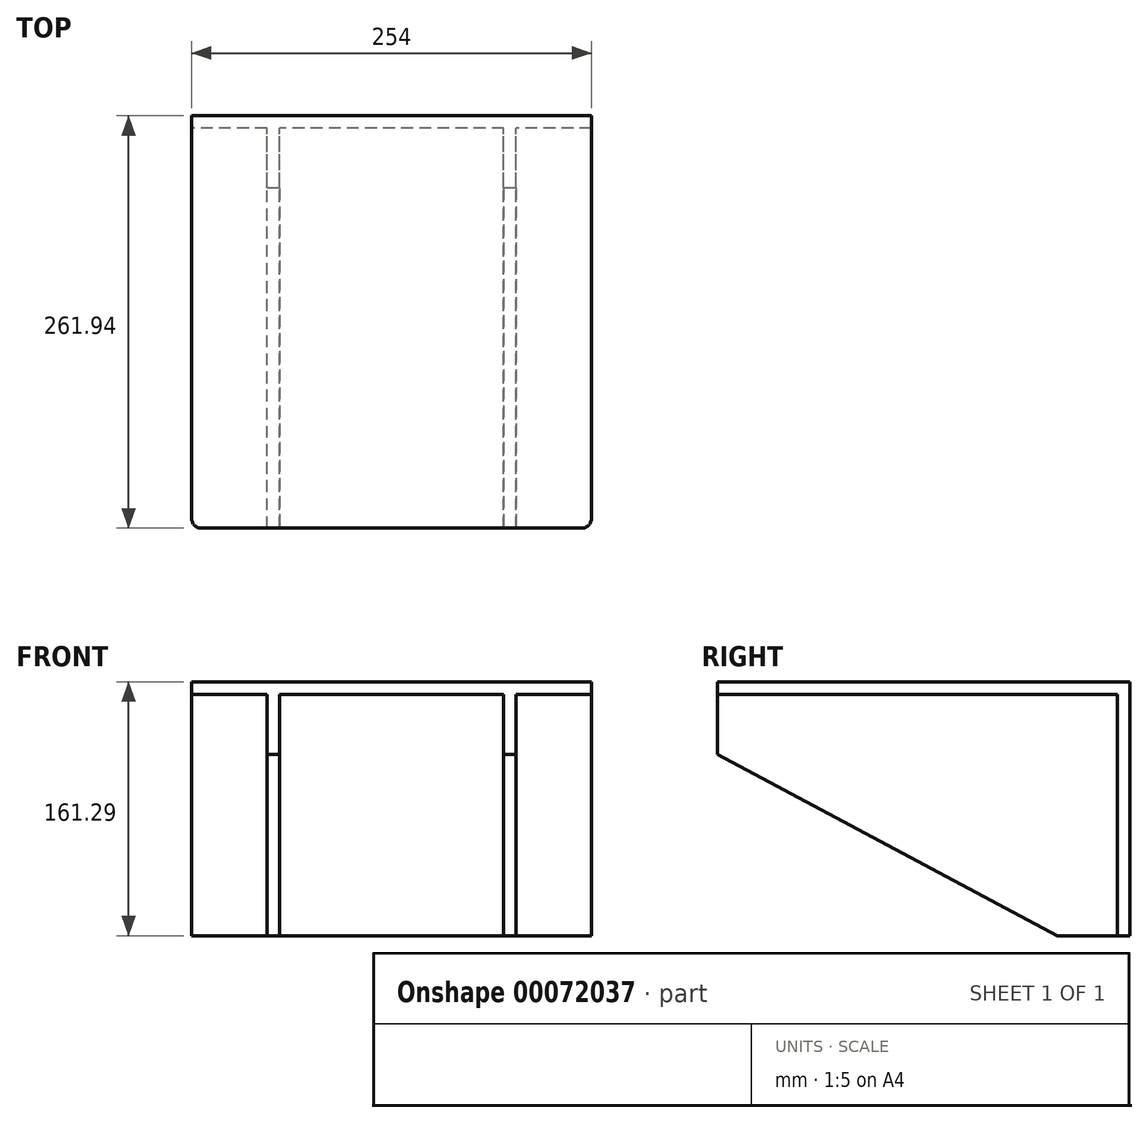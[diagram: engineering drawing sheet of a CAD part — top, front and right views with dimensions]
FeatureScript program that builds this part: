
annotation { "Feature Type Name" : "Feature", "Feature Type Description" : "" }
export const myFeature = defineFeature(function(context is Context, id is Id, definition is map)
    precondition{}
    {
        {
            var Q0;
            Q0=qCreatedBy(makeId("Front.planeOp"),FACE);
            var sketch = newSketch(context, id + "F0", { "sketchPlane" : qUnion([Q0])});
            skLineSegment(sketch, "E0.bottom", {"start": v(127, 80.65) * mm, "end": v(-127, 80.65) * mm});
            skLineSegment(sketch, "E0.top", {"start": v(127, -80.65) * mm, "end": v(-127, -80.65) * mm});
            skLineSegment(sketch, "E0.left", {"start": v(127, 80.65) * mm, "end": v(127, -80.65) * mm});
            skLineSegment(sketch, "E0.right", {"start": v(-127, 80.65) * mm, "end": v(-127, -80.65) * mm});
            skPoint(sketch, "E0.middle", {"position": v(0, 0) * mm});
            skSolve(sketch);
        }
        {
            var Q0;
            Q0=makeQuery(id+"F0.imprint","IMPRINT",FACE,{"disambiguationData":[TD([[makeQuery(id+"F0.imprint","IMPRINT",EDGE,{"derivedFrom":sQuery(id+"F0.wireOp",EDGE,"E0.bottom")}),1.0]])]});
            extrude(context, id + "F1", {"entities" : qUnion([Q0]), "depth" : 7.94 * mm});
        }
        {
            var Q0;
            Q0=makeQuery(id+"F1.opExtrude","CAP_FACE",FACE,{"disambiguationData":[OSD([sQuery(id+"F0.wireOp",EDGE,"E0.bottom"),sQuery(id+"F0.wireOp",EDGE,"E0.top"),sQuery(id+"F0.wireOp",EDGE,"E0.left"),sQuery(id+"F0.wireOp",EDGE,"E0.right")])],"isStart":false});
            var sketch = newSketch(context, id + "F2", { "sketchPlane" : qUnion([Q0])});
            skLineSegment(sketch, "E1.bottom", {"start": v(-127, 80.65) * mm, "end": v(127, 80.65) * mm});
            skLineSegment(sketch, "E1.top", {"start": v(-127, 72.7) * mm, "end": v(127, 72.7) * mm});
            skLineSegment(sketch, "E1.left", {"start": v(-127, 80.65) * mm, "end": v(-127, 72.7) * mm});
            skLineSegment(sketch, "E1.right", {"start": v(127, 80.65) * mm, "end": v(127, 72.7) * mm});
            skSolve(sketch);
        }
        {
            var Q0;
            Q0 = qSketchRegion(id + "F2", true);
            extrude(context, id + "F3", {"entities" : qUnion([Q0]), "operationType" : NewBodyOperationType.ADD, "depth" : 254 * mm});
        }
        {
            var Q0;
            Q0=qCreatedBy(makeId("Front.planeOp"),FACE);
            var sketch = newSketch(context, id + "F4", { "sketchPlane" : qUnion([Q0])});
            skPoint(sketch, "E2.middle", {"position": v(0, 0) * mm});
            skLineSegment(sketch, "E3.bottom", {"start": v(-101.6, 1.9) * mm, "end": v(101.6, 1.9) * mm});
            skLineSegment(sketch, "E3.top", {"start": v(-101.6, -61.6) * mm, "end": v(101.6, -61.6) * mm});
            skLineSegment(sketch, "E3.left", {"start": v(-101.6, 1.9) * mm, "end": v(-101.6, -61.6) * mm});
            skLineSegment(sketch, "E3.right", {"start": v(101.6, 1.9) * mm, "end": v(101.6, -61.6) * mm});
            skSolve(sketch);
        }
        {
            var Q0;
            Q0=makeQuery(id+"F3.boolean.opBoolean","MERGE",FACE,{"derivedFrom":[makeQuery(id+"F1.opExtrude","SWEPT_FACE",FACE,{"disambiguationData":[OSD([sQuery(id+"F0.wireOp",EDGE,"E0.bottom")])]}),makeQuery(id+"F3.opExtrude","SWEPT_FACE",FACE,{"disambiguationData":[OSD([sQuery(id+"F2.wireOp",EDGE,"E1.bottom")])]})]});
            var sketch = newSketch(context, id + "F5", { "sketchPlane" : qUnion([Q0])});
            skLineSegment(sketch, "E4.bottom", {"start": v(-50, -139.65) * mm, "end": v(50, -139.65) * mm});
            skLineSegment(sketch, "E4.top", {"start": v(-50, -240.25) * mm, "end": v(50, -240.25) * mm});
            skLineSegment(sketch, "E4.left", {"start": v(-50, -139.65) * mm, "end": v(-50, -240.25) * mm});
            skLineSegment(sketch, "E4.right", {"start": v(50, -139.65) * mm, "end": v(50, -240.25) * mm});
            skSolve(sketch);
        }
        {
            var Q0;
            Q0=makeQuery(id+"F1.opExtrude","CAP_FACE",FACE,{"disambiguationData":[OSD([sQuery(id+"F0.wireOp",EDGE,"E0.bottom"),sQuery(id+"F0.wireOp",EDGE,"E0.top"),sQuery(id+"F0.wireOp",EDGE,"E0.left"),sQuery(id+"F0.wireOp",EDGE,"E0.right")])],"isStart":false});
            var sketch = newSketch(context, id + "F6", { "sketchPlane" : qUnion([Q0])});
            skLineSegment(sketch, "E5.bottom", {"start": v(-79.1, 72.7) * mm, "end": v(-71.16, 72.7) * mm});
            skLineSegment(sketch, "E5.top", {"start": v(-79.1, -80.65) * mm, "end": v(-71.16, -80.65) * mm});
            skLineSegment(sketch, "E5.left", {"start": v(-79.1, 72.7) * mm, "end": v(-79.1, -80.65) * mm});
            skLineSegment(sketch, "E5.right", {"start": v(-71.16, 72.7) * mm, "end": v(-71.16, -80.65) * mm});
            skLineSegment(sketch, "E6.bottom", {"start": v(71.16, 72.7) * mm, "end": v(79.1, 72.7) * mm});
            skLineSegment(sketch, "E6.top", {"start": v(71.16, -80.65) * mm, "end": v(79.1, -80.65) * mm});
            skLineSegment(sketch, "E6.left", {"start": v(71.16, 72.7) * mm, "end": v(71.16, -80.65) * mm});
            skLineSegment(sketch, "E6.right", {"start": v(79.1, 72.7) * mm, "end": v(79.1, -80.65) * mm});
            skSolve(sketch);
        }
        {
            var Q0;
            Q0 = qSketchRegion(id + "F6", true);
            var Q1;
            Q1=makeQuery(id+"F3.opExtrude","CAP_FACE",FACE,{"disambiguationData":[OSD([sQuery(id+"F2.wireOp",EDGE,"E1.bottom"),sQuery(id+"F2.wireOp",EDGE,"E1.top"),sQuery(id+"F2.wireOp",EDGE,"E1.left"),sQuery(id+"F2.wireOp",EDGE,"E1.right")])],"isStart":false});
            extrude(context, id + "F7", {"entities" : qUnion([Q0]), "operationType" : NewBodyOperationType.ADD, "endBound" : BoundingType.UP_TO_SURFACE, "endBoundEntityFace" : qUnion([Q1]), "depth" : 25.4 * mm});
        }
        {
            var Q0;
            Q0=makeQuery(id+"F7.opExtrude","SWEPT_FACE",FACE,{"disambiguationData":[OSD([sQuery(id+"F6.wireOp",EDGE,"E5.left")])]});
            var sketch = newSketch(context, id + "F8", { "sketchPlane" : qUnion([Q0])});
            skLineSegment(sketch, "E7", {"start": v(261.94, 34.6) * mm, "end": v(46.04, -80.65) * mm});
            skLineSegment(sketch, "E8", {"start": v(46.04, -80.65) * mm, "end": v(261.94, -80.65) * mm});
            skLineSegment(sketch, "E9", {"start": v(261.94, -80.65) * mm, "end": v(261.94, 34.6) * mm});
            skSolve(sketch);
        }
        {
            var Q0;
            Q0 = qSketchRegion(id + "F8", true);
            extrude(context, id + "F9", {"entities" : qUnion([Q0]), "operationType" : NewBodyOperationType.REMOVE, "endBound" : BoundingType.THROUGH_ALL, "oppositeDirection" : true, "depth" : 25.4 * mm});
        }
        {
            var Q0;
            Q0=makeQuery(id+"F3.opExtrude","CAP_EDGE",EDGE,{"disambiguationData":[OSD([sQuery(id+"F2.wireOp",EDGE,"E1.left")])],"isStart":false});
            var Q1;
            Q1=makeQuery(id+"F3.opExtrude","CAP_EDGE",EDGE,{"disambiguationData":[OSD([sQuery(id+"F2.wireOp",EDGE,"E1.right")])],"isStart":false});
            fillet(context, id + "F10", {"entities" : qUnion([Q0, Q1]), "radius" : 6.35 * mm, "tangentPropagation" : true, "allowEdgeOverflow" : false});
        }
    });
